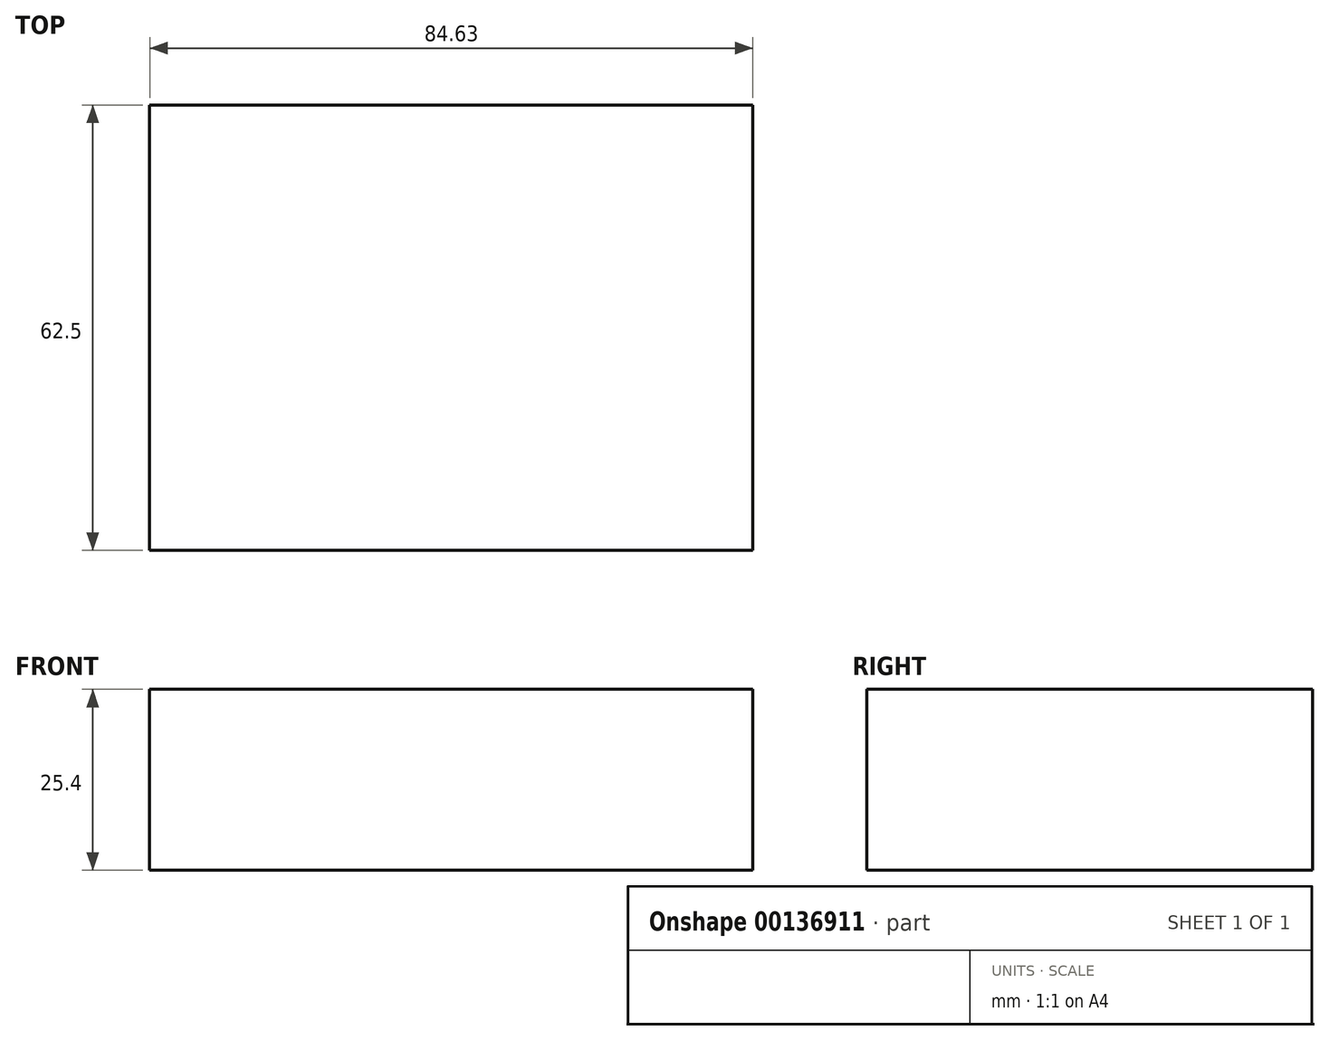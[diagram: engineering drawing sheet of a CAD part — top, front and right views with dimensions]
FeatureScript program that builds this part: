
annotation { "Feature Type Name" : "Feature", "Feature Type Description" : "" }
export const myFeature = defineFeature(function(context is Context, id is Id, definition is map)
    precondition{}
    {
        {
            var Q0;
            Q0=qCreatedBy(makeId("Top.planeOp"),FACE);
            var sketch = newSketch(context, id + "F0", { "sketchPlane" : qUnion([Q0])});
            skLineSegment(sketch, "E0.bottom", {"start": v(-37.83, -46.46) * mm, "end": v(46.8, -46.46) * mm});
            skLineSegment(sketch, "E0.top", {"start": v(-37.83, 16.04) * mm, "end": v(46.8, 16.04) * mm});
            skLineSegment(sketch, "E0.left", {"start": v(-37.83, -46.46) * mm, "end": v(-37.83, 16.04) * mm});
            skLineSegment(sketch, "E0.right", {"start": v(46.8, -46.46) * mm, "end": v(46.8, 16.04) * mm});
            skSolve(sketch);
        }
        {
            var Q0;
            Q0 = qSketchRegion(id + "F0", true);
            extrude(context, id + "F1", {"entities" : qUnion([Q0]), "flatOperationType" : FlatOperationType.REMOVE, "offsetDistance" : 25.4 * mm, "depth" : 25.4 * mm, "domain" : OperationDomain.MODEL});
        }
    });
